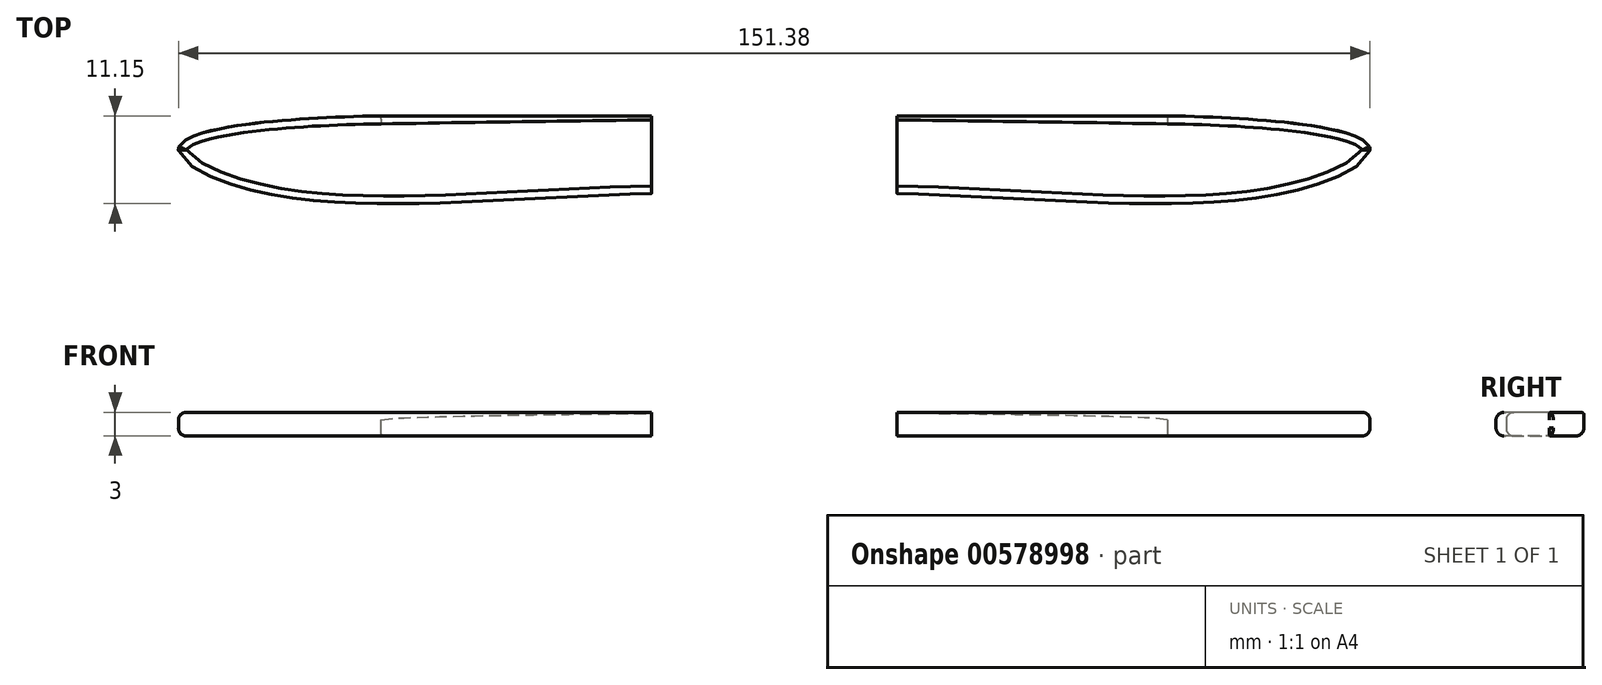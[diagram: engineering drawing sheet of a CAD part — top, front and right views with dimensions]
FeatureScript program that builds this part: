
annotation { "Feature Type Name" : "Feature", "Feature Type Description" : "" }
export const myFeature = defineFeature(function(context is Context, id is Id, definition is map)
    precondition{}
    {
        {
            var Q0;
            Q0=qCreatedBy(makeId("Top.planeOp"),FACE);
            var sketch = newSketch(context, id + "F0", { "sketchPlane" : qUnion([Q0])});
            skLineSegment(sketch, "E0", {"start": v(-15.62, 9.87) * mm, "end": v(-49.98, 9.87) * mm});
            skFitSpline(sketch, "E1", {"points": [v(-49.98, 9.87) * mm, v(-75.62, 5.96) * mm, v(-64.44, 0) * mm, v(-15.62, 0) * mm], "startDerivative": vector(-101.5, -1.46) * mm, "endDerivative": vector(117.9, 2.37) * mm});
            skLineSegment(sketch, "E2", {"start": v(-15.62, 9.87) * mm, "end": v(-15.62, 0) * mm});
            skLineSegment(sketch, "E3.MirrorCS", {"start": v(15.62, 9.87) * mm, "end": v(49.98, 9.87) * mm});
            skFitSpline(sketch, "E4.MirrorCS", {"points": [v(49.98, 9.87) * mm, v(75.62, 5.96) * mm, v(64.44, 0) * mm, v(15.62, 0) * mm], "startDerivative": vector(101.5, -1.46) * mm, "endDerivative": vector(-117.9, 2.37) * mm});
            skLineSegment(sketch, "E5.MirrorCS", {"start": v(15.62, 9.87) * mm, "end": v(15.62, 0) * mm});
            skSolve(sketch);
        }
        {
            var Q0;
            Q0=makeQuery(id+"F0.imprint","IMPRINT",FACE,{"disambiguationData":[TD([[makeQuery(id+"F0.imprint","IMPRINT",EDGE,{"derivedFrom":sQuery(id+"F0.wireOp",EDGE,"E0")}),1.0]])]});
            extrude(context, id + "F1", {"entities" : qUnion([Q0]), "depth" : 3 * mm, "offsetDistance" : 25 * mm});
        }
        {
            var Q0;
            Q0=makeQuery(id+"F1.opExtrude","CAP_EDGE",EDGE,{"disambiguationData":[OSD([sQuery(id+"F0.wireOp",EDGE,"E1")])],"isStart":false});
            fillet(context, id + "F2", {"entities" : qUnion([Q0]), "radius" : 1 * mm, "allowEdgeOverflow" : false});
        }
        {
            var Q0;
            Q0=makeQuery(id+"F1.opExtrude","CAP_EDGE",EDGE,{"disambiguationData":[OSD([sQuery(id+"F0.wireOp",EDGE,"E1")])],"isStart":true});
            var Q1;
            Q1=makeQuery(id+"F1.opExtrude","CAP_EDGE",EDGE,{"disambiguationData":[OSD([sQuery(id+"F0.wireOp",EDGE,"E0")])],"isStart":true});
            fillet(context, id + "F3", {"entities" : qUnion([Q0, Q1]), "radius" : 1 * mm, "tangentPropagation" : true, "allowEdgeOverflow" : false});
        }
        {
            var Q0;
            Q0=makeQuery(id+"F1.opExtrude","SWEPT_BODY",BODY,{"disambiguationData":[OSD([sQuery(id+"F0.wireOp",EDGE,"E0"),sQuery(id+"F0.wireOp",EDGE,"E1"),sQuery(id+"F0.wireOp",EDGE,"E2")])]});
            var Q1;
            Q1=qCreatedBy(makeId("Right.planeOp"),FACE);
            mirror(context, id + "F4", {"entities" : qUnion([Q0]), "mirrorPlane" : qUnion([Q1])});
        }
    });
